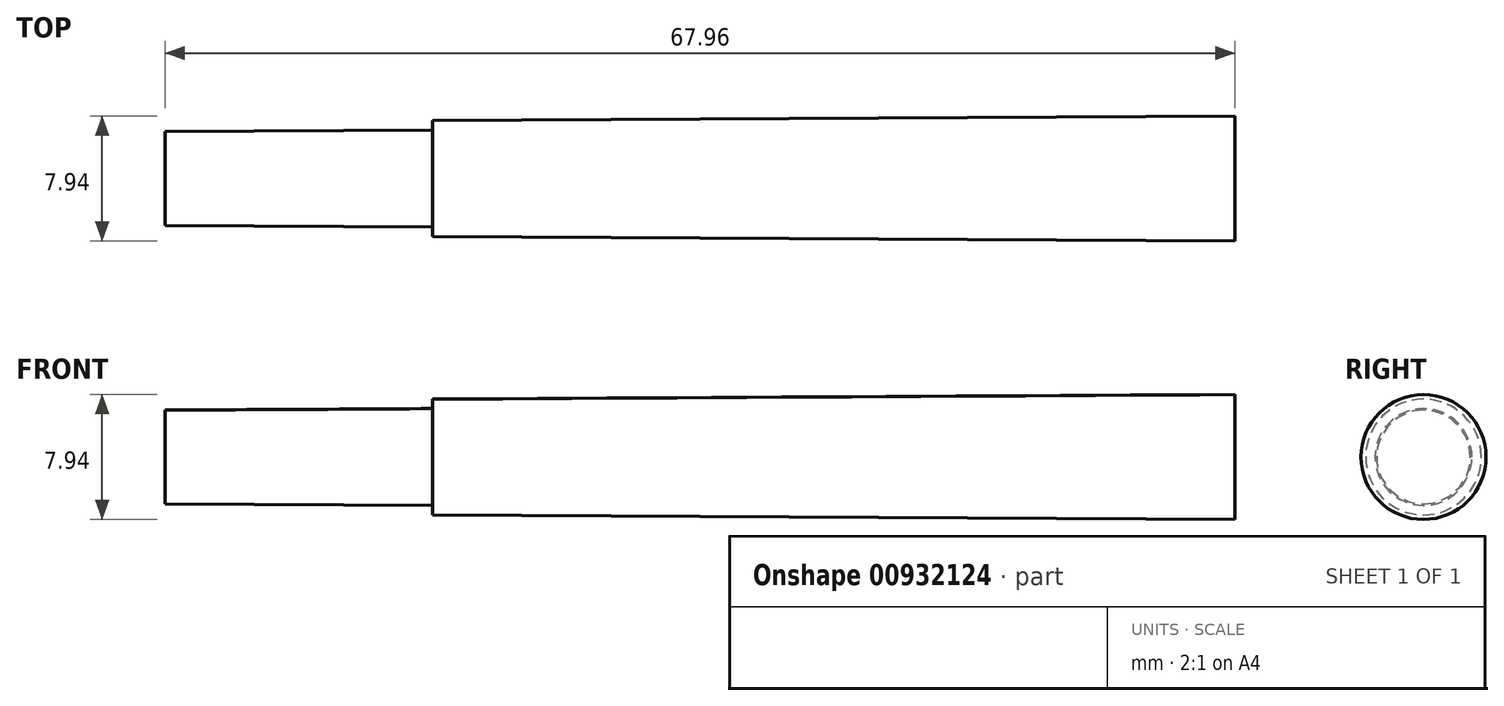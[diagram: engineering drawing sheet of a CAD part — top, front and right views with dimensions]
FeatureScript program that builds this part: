
annotation { "Feature Type Name" : "Feature", "Feature Type Description" : "" }
export const myFeature = defineFeature(function(context is Context, id is Id, definition is map)
    precondition{}
    {
        {
            var Q0;
            Q0=qCreatedBy(makeId("Top.planeOp"),FACE);
            var sketch = newSketch(context, id + "F0", { "sketchPlane" : qUnion([Q0])});
            skLineSegment(sketch, "E0", {"start": v(0, 0) * mm, "end": v(0, 3.43) * mm, "construction": true});
            skLineSegment(sketch, "E1", {"start": v(0, 0) * mm, "end": v(48.9, 0) * mm, "construction": true});
            skLineSegment(sketch, "E2", {"start": v(48.9, 0) * mm, "end": v(31.9, 0) * mm, "construction": true});
            skLineSegment(sketch, "E3", {"start": v(48.9, 0) * mm, "end": v(63.9, 0) * mm, "construction": true});
            skLineSegment(sketch, "E4", {"start": v(63.9, 0) * mm, "end": v(83.9, 0) * mm, "construction": true});
            skLineSegment(sketch, "E5", {"start": v(31.9, 0) * mm, "end": v(31.9, 3.58) * mm});
            skLineSegment(sketch, "E6", {"start": v(63.9, 0) * mm, "end": v(63.9, 3.76) * mm});
            skLineSegment(sketch, "E7", {"start": v(83.9, 0) * mm, "end": v(83.9, 3.88) * mm});
            skSolve(sketch);
        }
        {
            var Q0;
            Q0=qCreatedBy(makeId("Top.planeOp"),FACE);
            var sketch = newSketch(context, id + "F1", { "sketchPlane" : qUnion([Q0])});
            skLineSegment(sketch, "E8.0", {"start": v(0, 0) * mm, "end": v(0, 3.43) * mm});
            skLineSegment(sketch, "E9.0", {"start": v(31.9, 0) * mm, "end": v(31.9, 3.58) * mm});
            skLineSegment(sketch, "E10.0", {"start": v(83.9, 0) * mm, "end": v(83.9, 3.88) * mm});
            skLineSegment(sketch, "E11", {"start": v(83.9, 3.88) * mm, "end": v(31.9, 3.58) * mm, "construction": true});
            skPoint(sketch, "E12.0", {"position": v(48.9, 0) * mm});
            skLineSegment(sketch, "E13", {"start": v(48.9, 0) * mm, "end": v(48.9, 3.67) * mm});
            skLineSegment(sketch, "E14", {"start": v(31.9, 3.58) * mm, "end": v(48.9, 3.67) * mm, "construction": true});
            skLineSegment(sketch, "E15.0", {"start": v(31.9, 2.98) * mm, "end": v(48.9, 3.07) * mm});
            skLineSegment(sketch, "E16", {"start": v(48.9, 3.67) * mm, "end": v(48.9, 3.07) * mm});
            skLineSegment(sketch, "E17", {"start": v(48.9, 3.67) * mm, "end": v(83.9, 3.88) * mm});
            skLineSegment(sketch, "E18", {"start": v(83.9, 3.87) * mm, "end": v(99.86, 3.97) * mm});
            skLineSegment(sketch, "E19", {"start": v(31.9, 0) * mm, "end": v(99.86, 0) * mm});
            skLineSegment(sketch, "E20", {"start": v(99.86, 0) * mm, "end": v(99.86, 3.97) * mm});
            skLineSegment(sketch, "E21", {"start": v(31.9, 0) * mm, "end": v(31.9, 2.98) * mm});
            skSolve(sketch);
        }
        {
            var Q0;
            {var subQ5=sQuery(id+"F1.wireOp",EDGE,"E21");Q0=makeQuery(id+"F1.imprint","IMPRINT",FACE,{"disambiguationData":[TD([[makeQuery(id+"F1.imprint","IMPRINT",EDGE,{"derivedFrom":subQ5}),-1.0]])]});}
            var Q1;
            {var subQ6=sQuery(id+"F1.wireOp",EDGE,"E10.0");Q1=makeQuery(id+"F1.imprint","IMPRINT",FACE,{"disambiguationData":[TD([[makeQuery(id+"F1.imprint","IMPRINT",EDGE,{"derivedFrom":subQ6}),1.0]])]});}
            var Q2;
            {var subQ0=sQuery(id+"F1.wireOp",EDGE,"E10.0");Q2=makeQuery(id+"F1.imprint","IMPRINT",FACE,{"disambiguationData":[TD([[makeQuery(id+"F1.imprint","IMPRINT",EDGE,{"derivedFrom":subQ0}),-1.0]])]});}
            var Q3;
            Q3=sQuery(id+"F1.wireOp",EDGE,"E15.0");
            var Q4;
            Q4=sQuery(id+"F1.wireOp",EDGE,"E17");
            var Q5;
            Q5=sQuery(id+"F1.wireOp",EDGE,"E16");
            var Q6;
            Q6=sQuery(id+"F0.wireOp",EDGE,"E1");
            revolve(context, id + "F2", {"surfaceOperationType" : NewSurfaceOperationType.NEW, "entities" : qUnion([Q0, Q1, Q2]), "surfaceEntities" : qUnion([Q3, Q4, Q5]), "axis" : qUnion([Q6]), "revolveType" : RevolveType.FULL});
        }
    });
